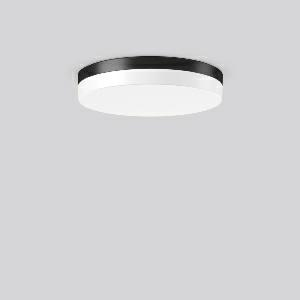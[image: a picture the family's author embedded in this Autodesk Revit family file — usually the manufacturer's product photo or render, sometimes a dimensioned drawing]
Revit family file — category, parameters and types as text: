
# Revit family: flat_slim_round_312632_0031_1_76_e566
name_source: partatom
category: Lighting Fixtures
units: mm (PartAtom-declared; Revit-internal decimal feet)

## family parameters
Cut with Voids When Loaded = No
Host = Face
Light Source = No
Part Type = Normal
Room Calculation Point = No
Round Connector Dimension = Use Diameter
Shared = No

## types (1)
- MultiLumen 1 830 (1 x LED Modul 830, 2450 lm, 3000)
    Apparent Load = 18 VA
    CIE Flux Codes = 37 67 88 84 100
    Color Rendering = 80
    Color Temperature = 3000
    Default Elevation = 1800 mm
    Height = 70 mm
    Lamp = 1 x LED Modul 830
    Lamp Light Flux = 2450 lm
    Lamp count = 1
    Length = 400 mm
    Lifetime = 50000 h
    Luminous efficacy = 136 lm/W
    Manufacturer = RZB
    ModVariant = No
    Model = 312632.0031.1.76
    Mounting Place = Ceiling
    Mounting Type = Surface mounted
    Number of Poles = 1
    OnlyDefault = Yes
    Power Factor = 1
    Product Name = FLAT SLIM round
    Product group = Surface mounted ceiling and wall luminaires
    ProductGroupID = 305
    Protection Class = Protection class I
    Protection Degree = Degree of protection
    RLX_Detail_Level = 1
    RLX_Emergency_Light_Flux = 0 lm
    RLX_Emergency_Type = 0
    RLX_Emergency_Type_DB = No
    RlxData = <blob elided: 21309 chars, md5=197e4192>
    Socket = socket
    Standby Power = 0 W
    System Light Flux = 2450 lm
    System Power = 18 W
    Type Comments = MultiLumen 1 830
    Type Image = 312631.0031.jpg
    URL = http://relux.com
    VarID = multilumen_1_830
    Voltage = 0 V
    Weight = 0.00 kg
    Width = 0 mm  [stored 0 ft]

note: [stored X ft] marks values corroborated as IEEE doubles in the binary element streams (Revit-internal decimal feet)

## geometry (parser evidence)
native form markers: Blend x4, Sweep x12
no freeform markers — native parametric forms only
